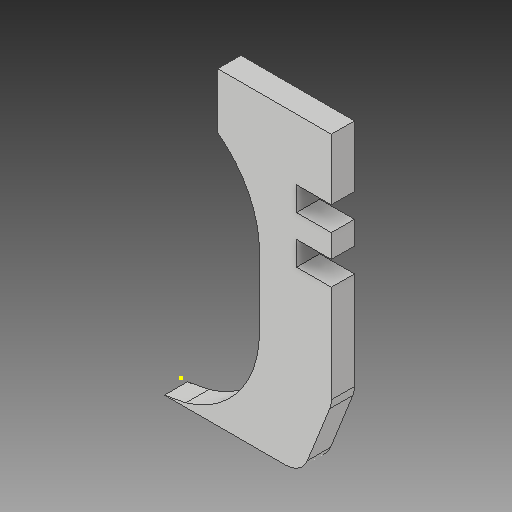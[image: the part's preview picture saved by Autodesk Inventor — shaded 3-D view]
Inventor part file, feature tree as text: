
AUTODESK INVENTOR PART (.ipt)
format: ipt  version: 2017 (Build 210142000, 142)  size: 115,712 bytes
history: native  units: in
note: dims shown in document units (in); Inventor stores cm internally (conversion verified against a paired STEP export)
features: sketch x4, other x3
ambient origin geometry x8: Origin, YZ Plane, XZ Plane, XY Plane, X Axis, Y Axis, Z Axis, Center Point
bodies: Solid1 (feature_tree)
feature tree (7):
  other  "Finger_MIR1.ipt"
  other  "Solid1::Finger_MIR1.ipt"
  other  "TaggingFeature1"
  sketch  "Sketch1"  dims[d0=0.3937in]
  sketch  "Sketch2"
  sketch  "Sketch3"
  sketch  "Sketch4"
